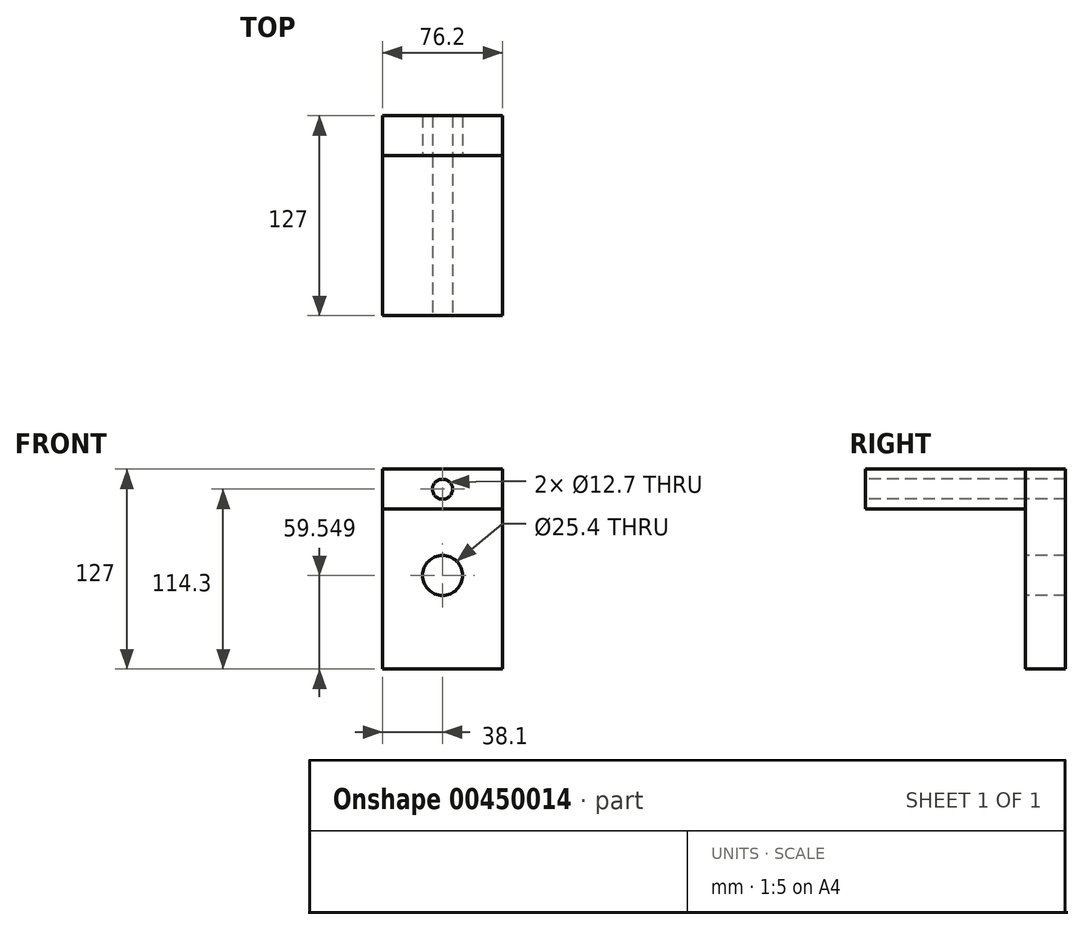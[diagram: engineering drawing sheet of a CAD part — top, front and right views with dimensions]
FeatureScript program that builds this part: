
annotation { "Feature Type Name" : "Feature", "Feature Type Description" : "" }
export const myFeature = defineFeature(function(context is Context, id is Id, definition is map)
    precondition{}
    {
        {
            var Q0;
            Q0=qCreatedBy(makeId("Top.planeOp"),FACE);
            var sketch = newSketch(context, id + "F0", { "sketchPlane" : qUnion([Q0])});
            skLineSegment(sketch, "E0.bottom", {"start": v(38.1, 12.7) * mm, "end": v(-38.1, 12.7) * mm});
            skLineSegment(sketch, "E0.top", {"start": v(38.1, -12.7) * mm, "end": v(-38.1, -12.7) * mm});
            skLineSegment(sketch, "E0.left", {"start": v(38.1, 12.7) * mm, "end": v(38.1, -12.7) * mm});
            skLineSegment(sketch, "E0.right", {"start": v(-38.1, 12.7) * mm, "end": v(-38.1, -12.7) * mm});
            skPoint(sketch, "E0.middle", {"position": v(0, 0) * mm});
            skSolve(sketch);
        }
        {
            var Q0;
            Q0 = qSketchRegion(id + "F0", true);
            extrude(context, id + "F1", {"entities" : qUnion([Q0]), "depth" : 127 * mm});
        }
        {
            var Q0;
            Q0=makeQuery(id+"F1.opExtrude","SWEPT_FACE",FACE,{"disambiguationData":[OSD([sQuery(id+"F0.wireOp",EDGE,"E0.top")])]});
            var sketch = newSketch(context, id + "F2", { "sketchPlane" : qUnion([Q0])});
            skCircle(sketch, "E1", {"center": v(0, 59.55) * mm, "radius": 12.7 * mm});
            skSolve(sketch);
        }
        {
            var Q0;
            Q0 = qSketchRegion(id + "F2", true);
            extrude(context, id + "F3", {"entities" : qUnion([Q0]), "operationType" : NewBodyOperationType.REMOVE, "endBound" : BoundingType.THROUGH_ALL, "oppositeDirection" : true, "depth" : 25.4 * mm});
        }
        {
            var Q0;
            Q0=makeQuery(id+"F1.opExtrude","SWEPT_FACE",FACE,{"disambiguationData":[OSD([sQuery(id+"F0.wireOp",EDGE,"E0.top")])]});
            var sketch = newSketch(context, id + "F4", { "sketchPlane" : qUnion([Q0])});
            skLineSegment(sketch, "E2.bottom", {"start": v(-38.1, 127) * mm, "end": v(38.1, 127) * mm});
            skLineSegment(sketch, "E2.top", {"start": v(-38.1, 101.6) * mm, "end": v(38.1, 101.6) * mm});
            skLineSegment(sketch, "E2.left", {"start": v(-38.1, 127) * mm, "end": v(-38.1, 101.6) * mm});
            skLineSegment(sketch, "E2.right", {"start": v(38.1, 127) * mm, "end": v(38.1, 101.6) * mm});
            skSolve(sketch);
        }
        {
            var Q0;
            Q0 = qSketchRegion(id + "F4", true);
            extrude(context, id + "F5", {"entities" : qUnion([Q0]), "depth" : 101.6 * mm});
        }
        {
            var Q0;
            Q0=makeQuery(id+"F5.opExtrude","CAP_FACE",FACE,{"disambiguationData":[OSD([sQuery(id+"F4.wireOp",EDGE,"E2.bottom"),sQuery(id+"F4.wireOp",EDGE,"E2.top"),sQuery(id+"F4.wireOp",EDGE,"E2.left"),sQuery(id+"F4.wireOp",EDGE,"E2.right")])],"isStart":false});
            var sketch = newSketch(context, id + "F6", { "sketchPlane" : qUnion([Q0])});
            skCircle(sketch, "E3", {"center": v(0, 114.3) * mm, "radius": 6.35 * mm});
            skSolve(sketch);
        }
        {
            var Q0;
            Q0 = qSketchRegion(id + "F6", true);
            extrude(context, id + "F7", {"entities" : qUnion([Q0]), "operationType" : NewBodyOperationType.REMOVE, "endBound" : BoundingType.THROUGH_ALL, "oppositeDirection" : true, "depth" : 25.4 * mm});
        }
        {
            var Q0;
            Q0=makeQuery(id+"F1.opExtrude","SWEPT_FACE",FACE,{"disambiguationData":[OSD([sQuery(id+"F0.wireOp",EDGE,"E0.top")])]});
            var sketch = newSketch(context, id + "F8", { "sketchPlane" : qUnion([Q0])});
            skCircle(sketch, "E4", {"center": v(0, 114.3) * mm, "radius": 6.35 * mm});
            skSolve(sketch);
        }
        {
            var Q0;
            Q0 = qSketchRegion(id + "F8", true);
            extrude(context, id + "F9", {"entities" : qUnion([Q0]), "operationType" : NewBodyOperationType.REMOVE, "endBound" : BoundingType.THROUGH_ALL, "oppositeDirection" : true, "depth" : 25.4 * mm});
        }
    });
